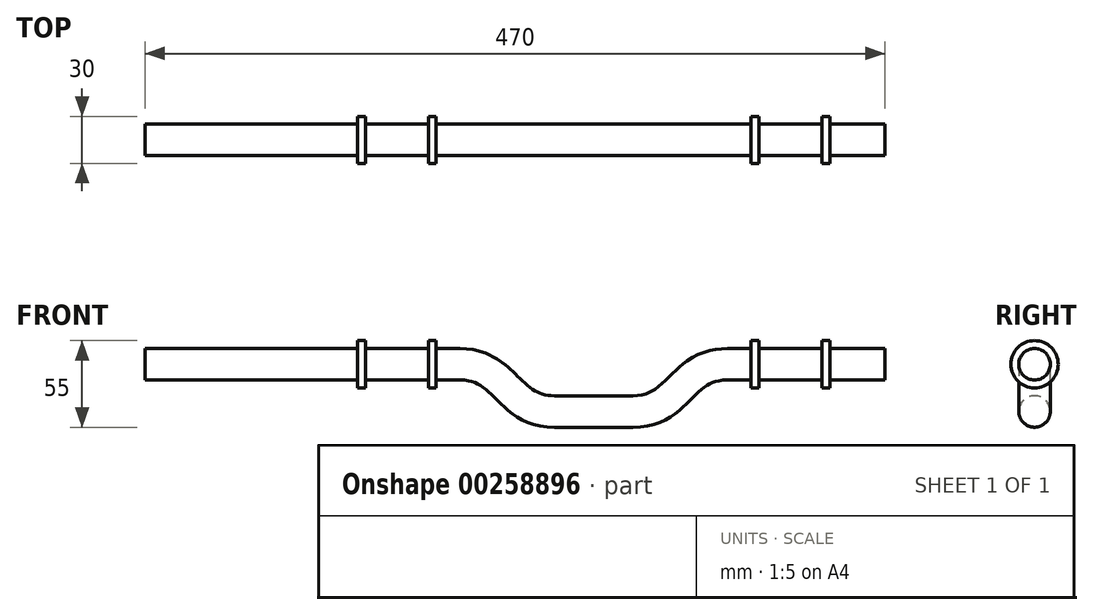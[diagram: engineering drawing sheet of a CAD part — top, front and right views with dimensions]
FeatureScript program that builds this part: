
annotation { "Feature Type Name" : "Feature", "Feature Type Description" : "" }
export const myFeature = defineFeature(function(context is Context, id is Id, definition is map)
    precondition{}
    {
        {
            var Q0;
            Q0=qCreatedBy(makeId("Front.planeOp"),FACE);
            var sketch = newSketch(context, id + "F0", { "sketchPlane" : qUnion([Q0])});
            skLineSegment(sketch, "E0", {"start": v(0, 0) * mm, "end": v(-200, 0) * mm});
            skLineSegment(sketch, "E1", {"start": v(60, -30) * mm, "end": v(110, -30) * mm});
            skLineSegment(sketch, "E2", {"start": v(0, 0) * mm, "end": v(30, 0) * mm, "construction": true});
            skLineSegment(sketch, "E3", {"start": v(30, 0) * mm, "end": v(30, -30) * mm, "construction": true});
            skLineSegment(sketch, "E4", {"start": v(30, -30) * mm, "end": v(60, -30) * mm, "construction": true});
            skFitSpline(sketch, "E5", {"points": [v(0, 0) * mm, v(60, -30) * mm], "startDerivative": vector(90, 0) * mm, "endDerivative": vector(90, 0) * mm});
            skLineSegment(sketch, "E6", {"start": v(110, -30) * mm, "end": v(140, -30) * mm, "construction": true});
            skLineSegment(sketch, "E7", {"start": v(140, -30) * mm, "end": v(140, 0) * mm, "construction": true});
            skLineSegment(sketch, "E8", {"start": v(140, 0) * mm, "end": v(170, 0) * mm, "construction": true});
            skFitSpline(sketch, "E9", {"points": [v(110, -30) * mm, v(170, 0) * mm], "startDerivative": vector(90, 0) * mm, "endDerivative": vector(90, 0) * mm});
            skLineSegment(sketch, "E10", {"start": v(170, 0) * mm, "end": v(270, 0) * mm});
            skLineSegment(sketch, "E11", {"start": v(-200, 0) * mm, "end": v(-200, -10) * mm});
            skLineSegment(sketch, "E12", {"start": v(0, -10) * mm, "end": v(0, 0) * mm});
            skLineSegment(sketch, "E13", {"start": v(170, 0) * mm, "end": v(170, -10) * mm});
            skLineSegment(sketch, "E14", {"start": v(270, -10) * mm, "end": v(270, 0) * mm});
            skLineSegment(sketch, "E15", {"start": v(0, -10) * mm, "end": v(-15, -10) * mm});
            skLineSegment(sketch, "E16", {"start": v(-15, -10) * mm, "end": v(-15, -15) * mm});
            skLineSegment(sketch, "E17", {"start": v(-15, -15) * mm, "end": v(-20, -15) * mm});
            skLineSegment(sketch, "E18", {"start": v(-20, -15) * mm, "end": v(-20, -10) * mm});
            skLineSegment(sketch, "E19", {"start": v(-20, -10) * mm, "end": v(-60, -10) * mm});
            skLineSegment(sketch, "E20", {"start": v(-60, -10) * mm, "end": v(-60, -15) * mm});
            skLineSegment(sketch, "E21", {"start": v(-60, -15) * mm, "end": v(-65, -15) * mm});
            skLineSegment(sketch, "E22", {"start": v(-65, -15) * mm, "end": v(-65, -10) * mm});
            skLineSegment(sketch, "E23", {"start": v(-65, -10) * mm, "end": v(-155, -10) * mm});
            skLineSegment(sketch, "E24", {"start": v(-155, -10) * mm, "end": v(-155, -15) * mm, "construction": true});
            skLineSegment(sketch, "E25", {"start": v(-155, -15) * mm, "end": v(-160, -15) * mm, "construction": true});
            skLineSegment(sketch, "E26", {"start": v(-160, -15) * mm, "end": v(-160, -10) * mm, "construction": true});
            skLineSegment(sketch, "E27", {"start": v(-160, -10) * mm, "end": v(-180, -10) * mm});
            skLineSegment(sketch, "E28", {"start": v(-180, -10) * mm, "end": v(-180, -15) * mm, "construction": true});
            skLineSegment(sketch, "E29", {"start": v(-180, -15) * mm, "end": v(-185, -15) * mm, "construction": true});
            skLineSegment(sketch, "E30", {"start": v(-185, -15) * mm, "end": v(-185, -10) * mm, "construction": true});
            skLineSegment(sketch, "E31", {"start": v(-185, -10) * mm, "end": v(-200, -10) * mm});
            skLineSegment(sketch, "E32", {"start": v(170, -10) * mm, "end": v(185, -10) * mm});
            skLineSegment(sketch, "E33", {"start": v(185, -10) * mm, "end": v(185, -15) * mm});
            skLineSegment(sketch, "E34", {"start": v(185, -15) * mm, "end": v(190, -15) * mm});
            skLineSegment(sketch, "E35", {"start": v(190, -15) * mm, "end": v(190, -10) * mm});
            skLineSegment(sketch, "E36", {"start": v(190, -10) * mm, "end": v(230, -10) * mm});
            skLineSegment(sketch, "E37", {"start": v(230, -10) * mm, "end": v(230, -15) * mm});
            skLineSegment(sketch, "E38", {"start": v(230, -15) * mm, "end": v(235, -15) * mm});
            skLineSegment(sketch, "E39", {"start": v(235, -15) * mm, "end": v(235, -10) * mm});
            skLineSegment(sketch, "E40", {"start": v(235, -10) * mm, "end": v(270, -10) * mm});
            skLineSegment(sketch, "E41", {"start": v(210, -10) * mm, "end": v(210, -110) * mm, "construction": true});
            skLineSegment(sketch, "E42", {"start": v(-40, -10) * mm, "end": v(-40, -110) * mm, "construction": true});
            skLineSegment(sketch, "E43", {"start": v(-40, -110) * mm, "end": v(210, -110) * mm, "construction": true});
            skLineSegment(sketch, "E44", {"start": v(-185, -10) * mm, "end": v(-180, -10) * mm});
            skLineSegment(sketch, "E45", {"start": v(-160, -10) * mm, "end": v(-155, -10) * mm});
            skSolve(sketch);
        }
        {
            var Q0;
            Q0=makeQuery(id+"F0.imprint","IMPRINT",FACE,{"disambiguationData":[TD([[makeQuery(id+"F0.imprint","IMPRINT",EDGE,{"derivedFrom":sQuery(id+"F0.wireOp",EDGE,"E0")}),1.0]])]});
            var Q1;
            Q1=makeQuery(id+"F0.imprint","IMPRINT",FACE,{"disambiguationData":[TD([[makeQuery(id+"F0.imprint","IMPRINT",EDGE,{"derivedFrom":sQuery(id+"F0.wireOp",EDGE,"E10")}),-1.0]])]});
            var Q2;
            Q2=sQuery(id+"F0.wireOp",EDGE,"E0");
            revolve(context, id + "F1", {"entities" : qUnion([Q0, Q1]), "axis" : qUnion([Q2]), "revolveType" : RevolveType.FULL});
        }
        {
            var Q0;
            Q0=makeQuery(id+"F1.opRevolve","SWEPT_FACE",FACE,{"disambiguationData":[OSD([sQuery(id+"F0.wireOp",EDGE,"E12")])]});
            var Q1;
            Q1=sQuery(id+"F0.wireOp",EDGE,"E5");
            var Q2;
            Q2=sQuery(id+"F0.wireOp",EDGE,"E1");
            var Q3;
            Q3=sQuery(id+"F0.wireOp",EDGE,"E9");
            sweep(context, id + "F2", {"operationType" : NewBodyOperationType.ADD, "profiles" : qUnion([Q0]), "path" : qUnion([Q1, Q2, Q3])});
        }
    });
